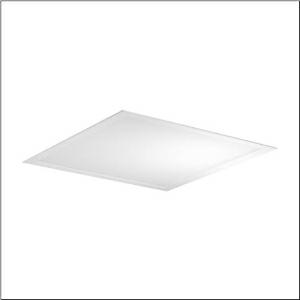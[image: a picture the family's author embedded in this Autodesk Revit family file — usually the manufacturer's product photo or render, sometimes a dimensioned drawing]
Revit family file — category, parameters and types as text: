
# Revit family: apollon_r__31_square_51mp11wd2342_576e
name_source: partatom
category: Lighting Fixtures
units: mm (PartAtom-declared; Revit-internal decimal feet)

## family parameters
Cut with Voids When Loaded = No
Host = Face
Light Source = No
Part Type = Normal
Room Calculation Point = No
Round Connector Dimension = Use Diameter
Shared = No

## types (1)
- Apollon® 31 square (1 x LED, 3800 lm, 27.5 W, 3000K)
    Apparent Load = 28 VA
    CIE Flux Codes = 61 87 97 100 100
    Color Rendering = 80
    Color Temperature = 3000K
    Default Elevation = 1800 mm
    Description = Apollon® 31 square, office luminaire, primary optical cover: micro prismatic cover, of PMMA, CAT 2 (L<= 3000cd/m²), light emission: direct distribution, primary light characteristic: symmetric, installation type: lay-in mounting, LED, rated luminous flux: 3.800lm, luminous efficacy: 138lm/W, light colour: 830, colour temperature: 3000K, control gear: DALI 2, Multilumen, with terminal, 5-pole, mains connection: 220..240V, AC/DC, 0/50..60Hz, rated input power: 28W, housing, of aluminium, traffic white (RAL 9016), module: M625, length: 620mm, width: 620mm, height: 62mm, recess depth: 180mm, housing upper side, of sheet steel, coated, protection rating (complete): IP20, protection rating (on room side): IP40, insulation class (complete): insulation class II (safety insulation), certification: CE, ENEC, impact resistance: IK03, permissible operating ambient temperature: -20..+40°C, permissible storage temperature: -20..+60°C, standard: EN 60598-2-22, packaging unit: 1 piece
    Height = 0 mm  [stored 0 ft]
    Lamp = 1 x LED
    Lamp Light Flux = 3800 lm
    Lamp Power = 27.5 W
    Lamp count = 1
    Length = 620 mm
    Luminous efficacy = 138 lm/W
    Manufacturer = Siteco
    ModVariant = No
    Model = 51MP11WD2342
    Mounting Place = Ceiling
    Mounting Type = Recessed
    Number of Poles = 1
    OnlyDefault = Yes
    Power Factor = 1
    Product Name = Apollon® 31 square
    Product group = office luminaire | ceiling recessed
    ProductGroupID = 401
    Protection Class = Protection class II
    Protection Degree = IP 20
    RLX_Detail_Level = 1
    RLX_Emergency_Light_Flux = 0 lm
    RLX_Emergency_Type = 0
    RLX_Emergency_Type_DB = No
    RlxData = <blob elided: 13033 chars, md5=052b7ba8>
    Socket = socket
    Standby Power = 0 W
    System Light Flux = 3800 lm
    System Power = 28 W
    Type Comments = Product without accessories
    Type Image = l_1291039.jpg
    URL = http://relux.com
    VarID = ---
    Voltage = 0 V
    Weight = 0.00 kg
    Width = 620 mm

note: [stored X ft] marks values corroborated as IEEE doubles in the binary element streams (Revit-internal decimal feet)

## geometry (parser evidence)
native form markers: Sweep x10
no freeform markers — native parametric forms only
